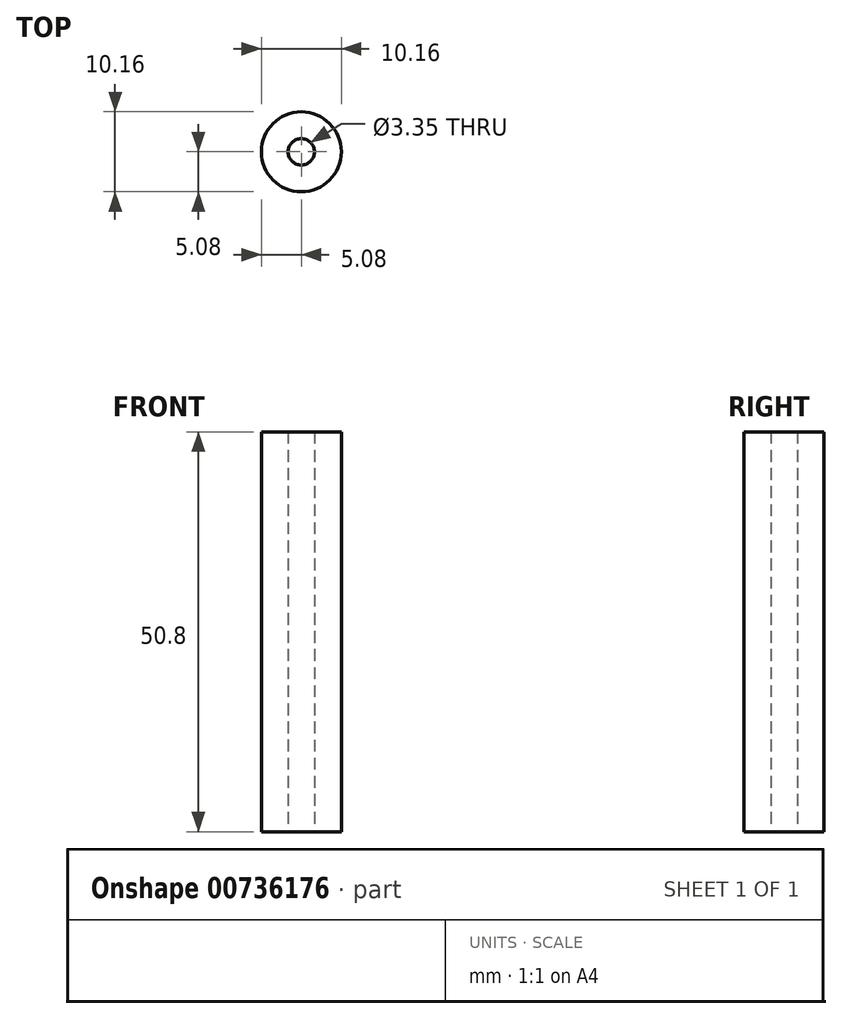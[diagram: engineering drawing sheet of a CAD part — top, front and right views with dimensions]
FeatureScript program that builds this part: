
annotation { "Feature Type Name" : "Feature", "Feature Type Description" : "" }
export const myFeature = defineFeature(function(context is Context, id is Id, definition is map)
    precondition{}
    {
        {
            var Q0;
            Q0=qCreatedBy(makeId("Top.planeOp"),FACE);
            var sketch = newSketch(context, id + "F0", { "sketchPlane" : qUnion([Q0])});
            skCircle(sketch, "E0", {"center": v(0, 0) * mm, "radius": 1.68 * mm});
            skCircle(sketch, "E1", {"center": v(0, 0) * mm, "radius": 5.08 * mm});
            skPoint(sketch, "E2", {"position": v(0, 5.08) * mm});
            skPoint(sketch, "E3", {"position": v(0, 1.68) * mm});
            skPoint(sketch, "E4", {"position": v(-5.08, 0) * mm});
            skPoint(sketch, "E5", {"position": v(5.08, 0) * mm});
            skPoint(sketch, "E6", {"position": v(0, -5.08) * mm});
            skSolve(sketch);
        }
        {
            var Q0;
            Q0=makeQuery(id+"F0.imprint","IMPRINT",FACE,{"disambiguationData":[TD([[makeQuery(id+"F0.imprint","IMPRINT",EDGE,{"derivedFrom":sQuery(id+"F0.wireOp",EDGE,"E0")}),-1.0]])]});
            var Q1;
            {var subQ0=sQuery(id+"F0.wireOp",EDGE,"mDm6WsvY-WrFa-lZOm-4hcX-e54av7ShyZpF");Q1=makeQuery(id+"F0.imprint","IMPRINT",FACE,{"disambiguationData":[TD([[makeQuery(id+"F0.imprint","IMPRINT",EDGE,{"derivedFrom":subQ0}),1.0]])]});}
            var Q2;
            {var subQ0=sQuery(id+"F0.wireOp",EDGE,"7uMMuGbc-kVnB-vpk6-6K8d-kGebzvzDoKNQ");Q2=makeQuery(id+"F0.imprint","IMPRINT",FACE,{"disambiguationData":[TD([[makeQuery(id+"F0.imprint","IMPRINT",EDGE,{"derivedFrom":subQ0}),-1.0]])]});}
            extrude(context, id + "F1", {"entities" : qUnion([Q0, Q1, Q2]), "depth" : 50.8 * mm, "offsetDistance" : 25.4 * mm});
        }
    });
